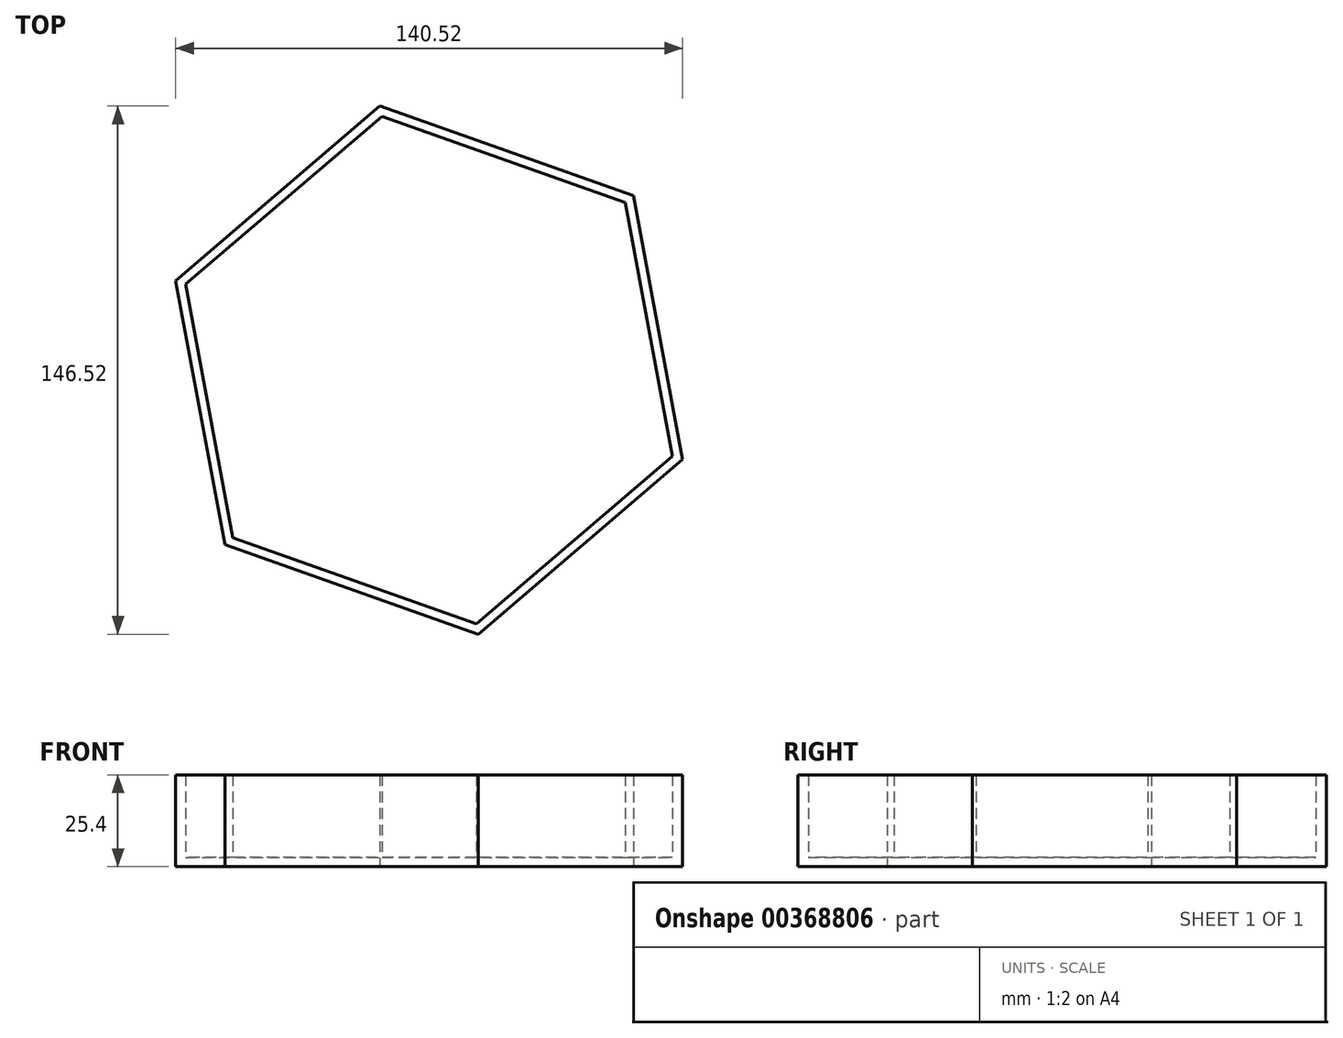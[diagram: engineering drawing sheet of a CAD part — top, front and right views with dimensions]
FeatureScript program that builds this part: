
annotation { "Feature Type Name" : "Feature", "Feature Type Description" : "" }
export const myFeature = defineFeature(function(context is Context, id is Id, definition is map)
    precondition{}
    {
        {
            var Q0;
            Q0=qCreatedBy(makeId("Top.planeOp"),FACE);
            var sketch = newSketch(context, id + "F0", { "sketchPlane" : qUnion([Q0])});
            skCircle(sketch, "E0", {"center": v(0, 0) * mm, "radius": 76.2 * mm});
            skSolve(sketch);
        }
        {
            var Q0;
            Q0=makeQuery(id+"F0.imprint","IMPRINT",FACE,{"disambiguationData":[TD([[makeQuery(id+"F0.imprint","IMPRINT",EDGE,{"derivedFrom":sQuery(id+"F0.wireOp",EDGE,"E0")}),1.0]])]});
            var sketch = newSketch(context, id + "F1", { "sketchPlane" : qUnion([Q0])});
            skCircle(sketch, "E1.cCircle", {"center": v(0, 0) * mm, "radius": 64.53 * mm, "construction": true});
            skLineSegment(sketch, "E1.0", {"start": v(-70.26, 24.82) * mm, "end": v(-13.64, 73.26) * mm});
            skLineSegment(sketch, "E1.1", {"start": v(-13.64, 73.26) * mm, "end": v(56.63, 48.44) * mm});
            skLineSegment(sketch, "E1.2", {"start": v(56.63, 48.44) * mm, "end": v(70.26, -24.82) * mm});
            skLineSegment(sketch, "E1.3", {"start": v(70.26, -24.82) * mm, "end": v(13.64, -73.26) * mm});
            skLineSegment(sketch, "E1.4", {"start": v(13.64, -73.26) * mm, "end": v(-56.63, -48.44) * mm});
            skLineSegment(sketch, "E1.5", {"start": v(-56.63, -48.44) * mm, "end": v(-70.26, 24.82) * mm});
            skPoint(sketch, "E1.0.midPoint", {"position": v(-41.95, 49.04) * mm});
            skSolve(sketch);
        }
        {
            var Q0;
            Q0 = qSketchRegion(id + "F1", true);
            extrude(context, id + "F2", {"entities" : qUnion([Q0]), "depth" : 25.4 * mm});
        }
        {
            var Q0;
            Q0=makeQuery(id+"F2.opExtrude","CAP_FACE",FACE,{"disambiguationData":[OSD([sQuery(id+"F1.wireOp",EDGE,"E1.0"),sQuery(id+"F1.wireOp",EDGE,"E1.1"),sQuery(id+"F1.wireOp",EDGE,"E1.2"),sQuery(id+"F1.wireOp",EDGE,"E1.3"),sQuery(id+"F1.wireOp",EDGE,"E1.4"),sQuery(id+"F1.wireOp",EDGE,"E1.5")])],"isStart":false});
            shell(context, id + "F3", {"entities" : qUnion([Q0]), "thickness" : 2.54 * mm});
        }
    });
